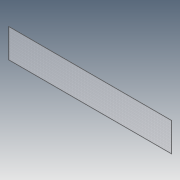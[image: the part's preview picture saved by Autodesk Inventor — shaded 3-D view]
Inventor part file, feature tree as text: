
AUTODESK INVENTOR PART (.ipt)
format: ipt  version: 2012 (Build 160160000, 160)  size: 91,136 bytes
history: native  units: in
note: dims shown in document units (in); Inventor stores cm internally (conversion verified against a paired STEP export)
features: extrude x2, sketch x1
ambient origin geometry x8: Origin, YZ Plane, XZ Plane, XY Plane, X Axis, Y Axis, Z Axis, Center Point
bodies: Solid1 (feature_tree)
feature tree (3):
  sketch  "Sketch1"  dims[d0=267.4in d1=48.0in d2=0.25in d3=0.0in d4=0.5in d5=0.5in d6=0.0in]
  extrude  "Extrusion1"  Depth=48.0in
  extrude  "Extrusion2"  Depth=0.25in TaperAngle=0.0deg
